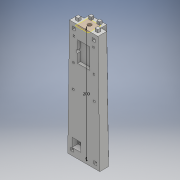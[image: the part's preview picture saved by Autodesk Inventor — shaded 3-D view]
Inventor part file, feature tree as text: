
AUTODESK INVENTOR PART (.ipt)
format: ipt  version: 2017 (Build 210142000, 142)  size: 478,720 bytes
history: native  units: mm
features: sketch x31, extrude x29, chamfer x8, loft x2, plane x1, hole x1
ambient origin geometry x8: Origin, YZ Plane, XZ Plane, XY Plane, X Axis, Y Axis, Z Axis, Center Point
bodies: Solid1 (feature_tree)
feature tree (72):
  sketch  "Sketch1"  dims[d0=55.0mm d1=15.0mm]
  sketch  "Sketch2"  dims[d2=12.5mm d3=35.0mm]
  sketch  "Sketch3"  dims[d4=10.0mm d5=200.0mm]
  plane  "Work Plane1"
  sketch  "Sketch4"  dims[d6=49.0mm d7=15.0mm]
  sketch  "Sketch5"  dims[d8=12.5mm d9=29.0mm]
  loft  "Loft1"
  loft  "Loft2"
  sketch  "Sketch9"  dims[d10=10.0mm d11=0.0mm d12=90.0deg]
  sketch  "Sketch10"  dims[d13=0.0mm d14=90.0deg d15=0.0mm d16=90.0deg]
  extrude  "Extrusion9"  Depth=200.0mm
  extrude  "Extrusion12"  Depth=15.0mm
  sketch  "Sketch18"  dims[d17=0.0mm d18=90.0deg d34=5.5mm]
  sketch  "Sketch19"  dims[d35=5.5mm d36=5.5mm]
  sketch  "Sketch20"  dims[d37=5.5mm d62=6.0mm d63=0.0mm]
  extrude  "Extrusion21"  Depth=29.0mm
  extrude  "Extrusion22"  TaperAngle=0.0deg  [1 undecoded]
  extrude  "Extrusion23"  TaperAngle=0.0deg  [1 undecoded]
  extrude  "Extrusion24"  Depth=5.5mm
  extrude  "Extrusion25"  Depth=5.5mm
  extrude  "Extrusion26"  Depth=6.0mm TaperAngle=0.0deg
  extrude  "Extrusion31"  Depth=2.0mm
  extrude  "Extrusion32"  TaperAngle=0.0deg  [1 undecoded]
  extrude  "Extrusion33"  TaperAngle=0.0deg  [1 undecoded]
  extrude  "Extrusion34"  Depth=1.2mm
  extrude  "Extrusion35"  Depth=2.8mm
  extrude  "Extrusion36"  Depth=8.0mm TaperAngle=0.0deg
  chamfer  "Chamfer3"  Distance=6.6mm
  chamfer  "Chamfer4"  Distance=8.0mm
  chamfer  "Chamfer5"  Distance=6.6mm
  chamfer  "Chamfer8"  Distance=8.0mm
  chamfer  "Chamfer9"  Distance=6.6mm
  chamfer  "Chamfer10"  Distance=8.0mm
  extrude  "Extrusion37"  TaperAngle=180.0deg  [1 undecoded]
  chamfer  "Chamfer11"  Distance=1.2mm
  extrude  "Extrusion38"  Depth=5.0mm TaperAngle=0.0deg
  extrude  "Extrusion39"  Depth=2.8mm
  chamfer  "Chamfer12"  Distance=2.8mm
  hole  "Hole2"  [1 undecoded]
  extrude  "Extrusion40"  Depth=2.0mm
  sketch  "Sketch46"  dims[d147=2.0mm]
  sketch  "Sketch47"  dims[d148=1.2mm]
  extrude  "Extrusion41"  TaperAngle=180.0deg  [1 undecoded]
  extrude  "Extrusion42"  Depth=1.2mm
  extrude  "Extrusion43"  Depth=1.2mm
  extrude  "Extrusion44"  Depth=5.0mm TaperAngle=0.0deg
  extrude  "Extrusion45"  Depth=2.8mm
  extrude  "Extrusion48"  Depth=2.8mm
  extrude  "Extrusion49"  Depth=8.0mm TaperAngle=0.0deg
  extrude  "Extrusion50"  Depth=0.8mm TaperAngle=45.0deg
  extrude  "Extrusion51"  Depth=0.8mm TaperAngle=45.0deg
  extrude  "Extrusion52"  Depth=0.8mm TaperAngle=45.0deg
  extrude  "Extrusion53"  Depth=0.8mm TaperAngle=45.0deg
  sketch  "Sketch22"  dims[d68=6.0mm d69=0.0mm d90=2.0mm]
  sketch  "Sketch23"  dims[d91=2.0mm d92=0.0mm]
  sketch  "Sketch24"  dims[d93=2.0mm d94=0.0mm]
  sketch  "Sketch30"  dims[d103=1.2mm d104=1.2mm]
  sketch  "Sketch31"  dims[d105=6.6mm d106=0.0mm d107=2.8mm]
  sketch  "Sketch32"  dims[d108=2.8mm d109=8.0mm d110=0.0mm]
  sketch  "Sketch33"  dims[d111=1.2mm]
  sketch  "Sketch34"  dims[d112=1.2mm d113=6.6mm d114=0.0mm]
  sketch  "Sketch35"  dims[d115=2.8mm]
  sketch  "Sketch38"  dims[d116=2.8mm d117=8.0mm d118=0.0mm]
  sketch  "Sketch40"  dims[d119=1.2mm]
  sketch  "Sketch41"  dims[d120=1.2mm d121=6.6mm d122=0.0mm]
  sketch  "Sketch42"  dims[d123=2.8mm]
  sketch  "Sketch44"  dims[d124=2.8mm d125=8.0mm d126=0.0mm]
  sketch  "Sketch48"  dims[d149=1.2mm d150=6.6mm d151=0.0mm]
  sketch  "Sketch49"  dims[d152=2.8mm]
  sketch  "Sketch51"  dims[d153=2.8mm d154=8.0mm d155=0.0mm]
  sketch  "Sketch54"  dims[d156=2.0mm d157=180.0deg]
  sketch  "Sketch55"  dims[d158=1.2mm d159=1.2mm d160=6.6mm d161=0.0mm d162=2.8mm d163=2.8mm d164=8.0mm d165=0.0mm d166=2.0mm d167=180.0deg d168=1.2mm d169=1.2mm d170=6.6mm d171=0.0mm d172=2.8mm d173=2.8mm d174=8.0mm d175=0.0mm d182=0.8mm d183=2.0mm d184=45.0deg d185=0.8mm d186=2.0mm d187=45.0deg d188=0.8mm d189=2.0mm d190=45.0deg d197=0.8mm d198=2.0mm d199=45.0deg d200=0.8mm d201=2.0mm d202=45.0deg d203=0.8mm d204=2.0mm d205=45.0deg d210=5.0mm d211=5.0mm d212=5.0mm d213=0.0mm d214=5.0mm d215=2.0mm d216=45.0deg d217=12.5mm d218=1.2mm d219=1.2mm d220=7.8mm d221=0.0mm d222=2.8mm d223=2.8mm d224=8.0mm d225=0.0mm d226=0.8mm d227=2.0mm d228=45.0deg d229=15.0mm d230=6.4mm d231=6.0mm d232=4.0mm d233=2.0mm d234=90.0deg d235=8.0mm d236=20.594885mm d237=21.0mm d238=35.0mm d239=5.0mm d240=0.0mm d241=7.5mm d242=9.0mm d243=5.0mm d244=5.0mm d245=7.5mm d246=9.0mm d247=5.0mm d248=5.0mm d249=7.5mm d250=9.0mm d251=5.0mm d252=5.0mm d253=7.5mm d254=9.0mm d255=5.0mm d256=5.0mm d257=6.0mm d258=0.0mm d259=6.0mm d260=0.0mm d261=6.0mm d262=0.0mm d263=7.5mm d264=9.0mm d265=5.0mm d266=5.0mm d267=6.0mm d268=0.0mm d269=5.0mm d270=5.0mm d271=0.0mm d284=4.75mm d285=4.75mm d286=5.5mm d287=5.5mm d288=6.0mm d289=0.0mm d290=4.75mm d291=4.75mm d292=5.5mm d293=5.5mm d294=6.0mm d295=0.0mm d296=5.0mm d297=5.0mm d298=5.0mm d299=5.0mm d300=5.0mm d301=0.0mm d302=5.0mm d303=5.0mm d304=5.0mm d305=5.0mm d306=5.0mm d307=0.0mm d308=4.5mm d309=4.5mm d310=5.0mm d311=0.0mm d312=4.5mm d313=4.5mm d314=5.0mm d315=0.0mm]
note: 7 required parameter values undecoded (feature->parameter linkage not recoverable at this tier; creation-order binding heuristic only, values carry confidence <= 0.55)
